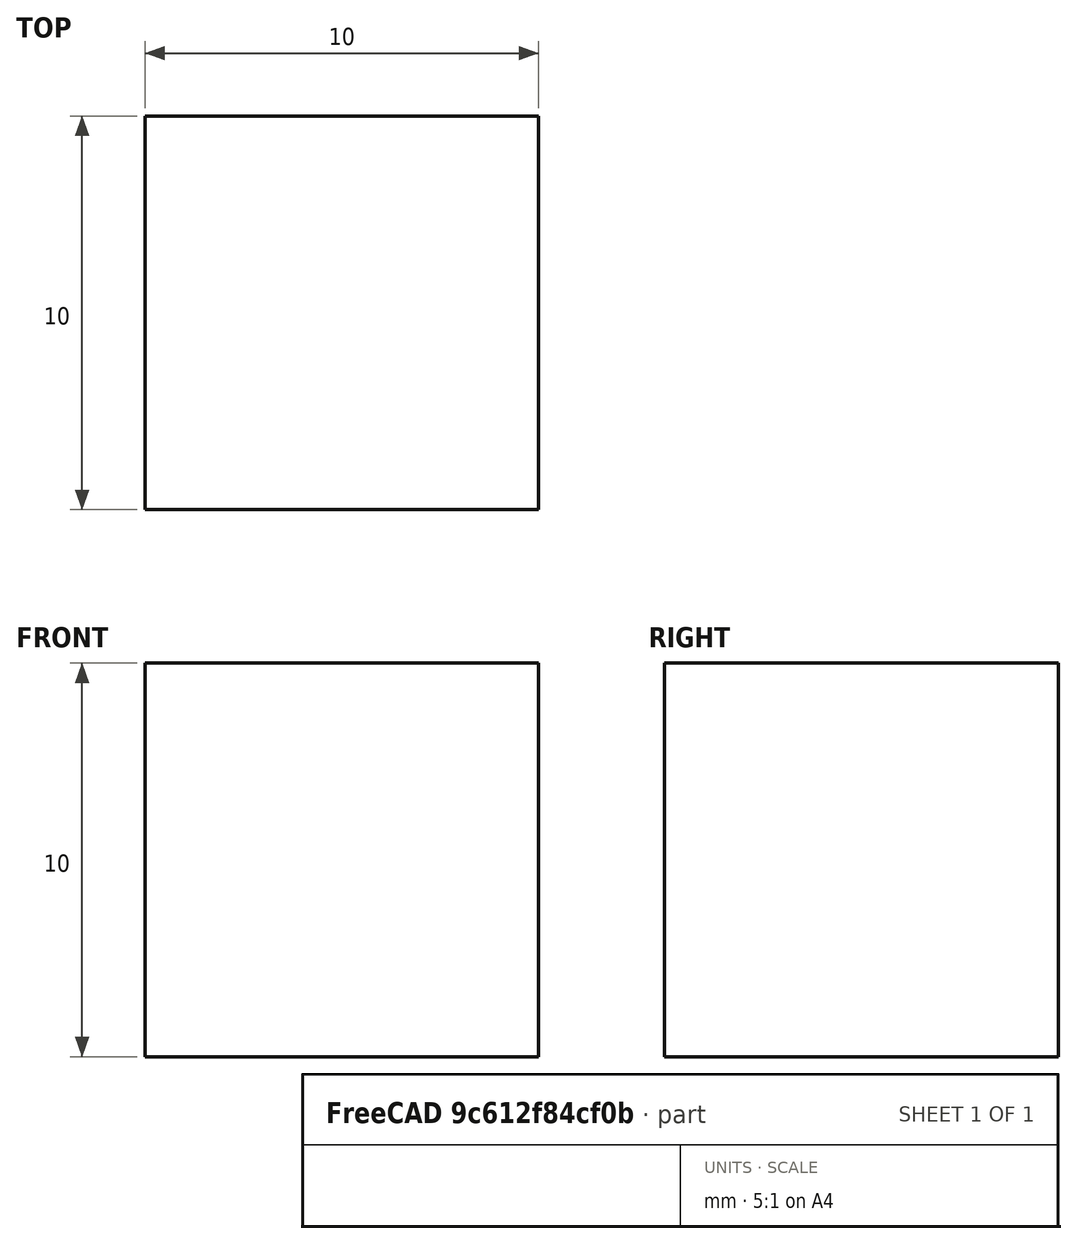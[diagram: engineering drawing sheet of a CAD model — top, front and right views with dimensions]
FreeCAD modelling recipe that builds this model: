
FCSTD DOCUMENT  (FreeCAD 0.21R33694 (Git))
Label: Shear Validation
License: All rights reserved
LicenseURL: http://en.wikipedia.org/wiki/All_rights_reserved
objects: Fem::ConstraintForce×6, Fem::FemMeshObjectPython×2, Fem::ConstraintDisplacement×2, Part::Box×1, Fem::FemSolverObjectPython×1, App::MaterialObjectPython×1, Fem::ConstraintFixed×1, Fem::FemResultObjectPython×1, Fem::FemAnalysis×1
note: 1 computed .brp shape members not serialized (recipe doc carries the construction recipe); baked Part::Feature solids carry a one-line shape summary decoded from their .brp

FEATURE [Part::Box] Box  label="Cube"
  AttacherType = Attacher::AttachEngine3D
  Height = 10
  Length = 10
  Width = 10
FEATURE [Fem::FemSolverObjectPython] SolverCcxTools  # FEM object (typed FeaturePython)
  AnalysisType = 0
  BeamShellResultOutput3D = false
  BucklingFactors = 1
  EigenmodeHighLimit = 1000000
  EigenmodeLowLimit = 0
  EigenmodesCount = 10
  GeometricalNonlinearity = 0
  IterationsControlParameterCutb = 0.25,0.5,0.75,0.85,,,1.5,
  IterationsControlParameterIter = 4,8,9,200,10,400,,200,,
  IterationsControlParameterTimeUse = false
  IterationsThermoMechMaximum = 2000
  IterationsUserDefinedIncrementations = false
  IterationsUserDefinedTimeStepLength = false
  MaterialNonlinearity = 0
  MatrixSolverType = 0
  SplitInputWriter = false
  ThermoMechSteadyState = true
  TimeEnd = 1
  TimeInitialStep = 0.01
FEATURE [App::MaterialObjectPython] MaterialSolid  # material (typed FeaturePython)
  Category = 0
  Material = AuthorAndLicense=(c) 2013 Yorik van Havre (CC-BY 3.0),CardName=Concrete-Generic,CompressiveStrength=25 MPa,Density=2400 kg/m^3,+7 more (map truncated)
FEATURE [Fem::FemMeshObjectPython] FEMMeshGmsh  # FEM object (typed FeaturePython)
  Algorithm2D = 0
  Algorithm3D = 0
  CharacteristicLengthMax = 0
  CharacteristicLengthMin = 10
  CoherenceMesh = true
  ElementDimension = 0
  ElementOrder = 1
  GeometryTolerance = 1e-06
  GroupsOfNodes = false
  HighOrderOptimize = 0
  MeshSizeFromCurvature = 12
  OptimizeNetgen = false
  OptimizeStd = true
  Part = -> Box
  RecombinationAlgorithm = 0
  Recombine3DAll = false
  RecombineAll = false
  SecondOrderLinear = false
FEATURE [Fem::ConstraintForce] ConstraintForce
  Direction = -> Box [Edge10]
  DirectionVector = (1,0,0)
  Force = 100
  NormalDirection = (0,0,1)
  Points = (9) [(0,0,10),(5,0,10),(10,0,10),(0,5,10),(5,5,10),(10,5,10),(0,10,10),(5,10,10),(10,10,10)]
  References = -> [Box]
FEATURE [Fem::ConstraintForce] ConstraintForce001
  Direction = -> Box [Edge5]
  DirectionVector = (0,0,1)
  Force = 100
  NormalDirection = (1,0,0)
  Points = (9) [(10,10,0),(10,10,5),(10,10,10),(10,5,0),(10,5,5),(10,5,10),(10,0,0),(10,0,5),(10,0,10)]
  References = -> [Box]
FEATURE [Fem::ConstraintForce] ConstraintForce002
  Direction = -> Box [Edge1]
  DirectionVector = (0,0,-1)
  Force = 100
  NormalDirection = (-1,0,0)
  Points = (9) [(0,10,0),(0,10,5),(0,10,10),(0,5,0),(0,5,5),(0,5,10),(0,0,0),(0,0,5),(0,0,10)]
  References = -> [Box]
  Reversed = true
FEATURE [Fem::ConstraintForce] ConstraintForce003
  Direction = -> Box [Edge9]
  DirectionVector = (-1,0,0)
  Force = 100
  NormalDirection = (0,0,-1)
  Points = (9) [(0,0,0),(5,0,0),(10,0,0),(0,5,0),(5,5,0),(10,5,0),(0,10,0),(5,10,0),(10,10,0)]
  References = -> [Box]
  Reversed = true
FEATURE [Fem::ConstraintFixed] ConstraintFixed
  NormalDirection = (0,0,1)
  Normals = (1) [(0,0,1)]
  Points = (1) [(0,0,0)]
  References = -> [Box]
  Scale = 2
FEATURE [Fem::ConstraintDisplacement] ConstraintDisplacement
  NormalDirection = (0,0,1)
  Normals = (1) [(0,0,1)]
  Points = (1) [(0,10,0)]
  References = -> [Box]
  Scale = 2
  hasXFormula = false
  hasYFormula = false
  hasZFormula = false
  rotxFix = false
  rotxFree = true
  rotyFix = false
  rotyFree = true
  rotzFix = false
  rotzFree = true
  useFlowSurfaceForce = false
  xDisplacement = 0
  xFix = false
  xFree = false
  xRotation = 0
  yDisplacement = 0
  yFix = false
  yFree = true
  yRotation = 0
  zDisplacement = 0
  zFix = false
  zFree = false
  zRotation = 0
FEATURE [Fem::ConstraintDisplacement] ConstraintDisplacement001
  NormalDirection = (0,0,1)
  Normals = (1) [(0,0,1)]
  Points = (1) [(10,0,0)]
  References = -> [Box]
  Scale = 2
  hasXFormula = false
  hasYFormula = false
  hasZFormula = false
  rotxFix = false
  rotxFree = true
  rotyFix = false
  rotyFree = true
  rotzFix = false
  rotzFree = true
  useFlowSurfaceForce = false
  xDisplacement = 0
  xFix = false
  xFree = true
  xRotation = 0
  yDisplacement = 0
  yFix = false
  yFree = true
  yRotation = 0
  zDisplacement = 0
  zFix = false
  zFree = false
  zRotation = 0
FEATURE [Fem::ConstraintForce] ConstraintForce004
  DirectionVector = (-1,0,0)
  Force = 1
  NormalDirection = (-1,0,0)
  Points = (9) [(0,10,0),(0,10,5),(0,10,10),(0,5,0),(0,5,5),(0,5,10),(0,0,0),(0,0,5),(0,0,10)]
  References = -> [Box]
FEATURE [Fem::ConstraintForce] ConstraintForce005
  DirectionVector = (1,0,0)
  Force = 1
  NormalDirection = (1,0,0)
  Points = (9) [(10,10,0),(10,10,5),(10,10,10),(10,5,0),(10,5,5),(10,5,10),(10,0,0),(10,0,5),(10,0,10)]
  References = -> [Box]
FEATURE [Fem::FemMeshObjectPython] Result_Mesh_Volume  # FEM object (typed FeaturePython)
FEATURE [Fem::FemResultObjectPython] ResultMechanical  # FEM object (typed FeaturePython)
  CriticalStrainRatio = [4.27358e-05,4.27358e-05,4.27358e-05,4.27358e-05,4.27358e-05,4.27358e-05,4.27358e-05,4.27358e-05,4.27358e-05,4.27358e-05,4.27358e-05,4.27358e-05,4.27358e-05,4.27358e-05,4.27358e-05,4.27358e-05,4.27358e-05,4.27358e-05,4.27358e-05,4.27358e-05,+43 more]
  DisplacementLengths = [0.00134653,0,0.00134653,3.69024e-19,0.00130966,8.43487e-05,0.00130966,8.43487e-05,0.000673264,0.00134653,0.000673264,1.2293e-18,0.000638653,0.00130966,0.000638653,8.43487e-05,4.21744e-05,0.00132755,4.21744e-05,0.00132755,0.000673264,+42 more]
  DisplacementVectors = (63) [(0.000622664,-2.20841e-17,0.00119391),(0,0,0),(0.000622664,-2.21558e-17,0.00119391),(0,-3.69024e-19,0),(0.000538316,-1.31549e-17,0.00119391),+58 more]
  Eigenmode = 0
  EigenmodeFrequency = 0
  Mesh = -> Result_Mesh_Volume
  NodeNumbers = [1,2,3,4,5,6,7,8,9,10,11,12,13,14,15,16,17,18,19,20,21,22,23,24,25,26,27,28,29,30,31,32,33,34,35,36,37,38,39,40,41,42,43,44,45,46,47,48,49,50,51,52,53,54,55,56,57,58,59,60,61,62,63]
  NodeStressXX = [0.0141391,0.0141391,0.0141391,0.0141391,0.0141391,0.0141391,0.0141391,0.0141391,0.0141391,0.0141391,0.0141391,0.0141391,0.0141391,0.0141391,0.0141391,0.0141391,0.0141391,0.0141391,0.0141391,0.0141391,0.0141391,0.0141391,0.0141391,0.0141391,+39 more]
  NodeStressXY = [-3.49327e-15,-1.24191e-15,2.73328e-15,5.56495e-15,5.43222e-15,-6.42056e-16,-7.44062e-15,-2.30648e-15,-2.36759e-15,-3.79995e-16,4.14912e-15,2.16152e-15,2.39508e-15,-1.0042e-15,-4.87355e-15,-1.47427e-15,-9.41981e-16,9.69476e-16,1.62924e-15,+44 more]
  NodeStressXZ = [1.40998,1.40998,1.40998,1.40998,1.40998,1.40998,1.40998,1.40998,1.40998,1.40998,1.40998,1.40998,1.40998,1.40998,1.40998,1.40998,1.40998,1.40998,1.40998,1.40998,1.40998,1.40998,1.40998,1.40998,1.40998,1.40998,1.40998,1.40998,1.40998,1.40998,+33 more]
  NodeStressYY = [4.00127e-15,1.73154e-15,3.52709e-15,4.05899e-15,4.57711e-15,-1.13069e-15,5.48003e-15,2.83196e-15,2.8664e-15,3.76418e-15,3.79304e-15,2.89526e-15,1.72321e-15,5.02857e-15,4.15599e-15,8.50631e-16,3.00421e-16,4.28919e-15,3.44547e-15,4.50356e-15,+43 more]
  NodeStressYZ = [6.83837e-16,-1.08866e-16,-6.56965e-16,-1.47396e-15,-1.26728e-15,1.47703e-16,1.94068e-15,7.49017e-16,2.87486e-16,1.34362e-17,-1.06546e-15,-7.91411e-16,-5.59788e-16,3.36699e-16,1.34485e-15,4.4836e-16,1.94184e-17,-2.91721e-16,-3.6247e-16,+44 more]
  NodeStressZZ = [0.000332299,0.000332299,0.000332299,0.000332299,0.000332299,0.000332299,0.000332299,0.000332299,0.000332299,0.000332299,0.000332299,0.000332299,0.000332299,0.000332299,0.000332299,0.000332299,0.000332299,0.000332299,0.000332299,0.000332299,+43 more]
  Peeq = [0.0122617,0.0122617,0.0122617,0.0122617,0.0122617,0.0122617,0.0122617,0.0122617,0.0122617,0.0122617,0.0122617,0.0122617,0.0122617,0.0122617,0.0122617,0.0122617,0.0122617,0.0122617,0.0122617,0.0122617,0.0122617,0.0122617,0.0122617,0.0122617,+39 more]
  PrincipalMax = [0,0,0,0,0,-4.04241e-16,0,0,0,0,0,0,-2.7883e-17,0,0,0,0,0,0,0,-1.14092e-15,0,-5.23102e-16,0,0,-1.2544e-15,-7.06345e-16,0,0,-2.002e-16,0,0,0,0,0,0,0,0,0,0,-7.55388e-16,0,-3.13159e-16,-5.62638e-16,-2.01999e-16,-2.17257e-15,-4.18247e-16,+16 more]
  PrincipalMin = [0.350825,0.350825,0.350825,0.350825,0.350825,0.350825,0.350825,0.350825,0.350825,0.350825,0.350825,0.350825,0.350825,0.350825,0.350825,0.350825,0.350825,0.350825,0.350825,0.350825,0.350825,0.350825,0.350825,0.350825,0.350825,0.350825,+37 more]
  ResultType = Fem::ResultMechanical
  Stats = [-8.43487e-05,0.000622664,-2.21558e-17,7.24321e-18,-3.23168e-18,0.00119391,0,0.00134653,0.354259,0.354259,-2.17257e-15,0,0,0,0.350825,0.350825,0,0,0.0122617,0.0122617,4.27358e-05,4.27358e-05,0,0,0,0]
  Temperature = [4.27358e-05,4.27358e-05,4.27358e-05,4.27358e-05,4.27358e-05,4.27358e-05,4.27358e-05,4.27358e-05,4.27358e-05,4.27358e-05,4.27358e-05,4.27358e-05,4.27358e-05,4.27358e-05,4.27358e-05,4.27358e-05,4.27358e-05,4.27358e-05,4.27358e-05,4.27358e-05,+43 more]
  Time = 0
  vonMises = [0.354259,0.354259,0.354259,0.354259,0.354259,0.354259,0.354259,0.354259,0.354259,0.354259,0.354259,0.354259,0.354259,0.354259,0.354259,0.354259,0.354259,0.354259,0.354259,0.354259,0.354259,0.354259,0.354259,0.354259,0.354259,0.354259,+37 more]
FEATURE [Fem::FemAnalysis] Analysis
  Group = -> [SolverCcxTools,MaterialSolid,FEMMeshGmsh,ConstraintForce,ConstraintForce001,ConstraintForce002,ConstraintForce003,ConstraintFixed,ConstraintDisplacement,ConstraintDisplacement001,ConstraintForce004,ConstraintForce005,ResultMechanical]
